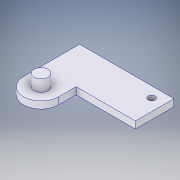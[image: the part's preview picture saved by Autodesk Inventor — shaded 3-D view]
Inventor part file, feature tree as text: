
AUTODESK INVENTOR PART (.ipt)
format: ipt  version: 2017 (Build 210142000, 142)  size: 130,560 bytes
history: native  units: in
note: dims shown in document units (in); Inventor stores cm internally (conversion verified against a paired STEP export)
features: extrude x3, sketch x3
ambient origin geometry x8: Origin, YZ Plane, XZ Plane, XY Plane, X Axis, Y Axis, Z Axis, Center Point
bodies: Solid1 (feature_tree)
feature tree (6):
  extrude  "Extrusion1"  TaperAngle=90.0deg  [1 undecoded]
  extrude  "Extrusion2"  Depth=1.0in
  extrude  "Extrusion3"  Depth=0.5906in
  sketch  "Sketch3"  dims[d6=2.3622in d7=90.0deg]
  sketch  "Sketch4"  dims[d8=0.4929in d9=1.0in]
  sketch  "Sketch5"  dims[d10=0.2953in d11=0.5906in d12=0.2362in d13=0.9456in d14=0.1181in d15=0.0in d16=0.315in d17=0.0in d18=0.1969in d19=0.4724in d20=0.4724in d21=0.1181in d22=0.1181in d23=1.0in d24=0.0in]
note: 1 required parameter value undecoded (feature->parameter linkage not recoverable at this tier; creation-order binding heuristic only, values carry confidence <= 0.55)
